annotation { "Feature Type Name" : "Feature", "Feature Type Description" : "" }
export const myFeature = defineFeature(function(context is Context, id is Id, definition is map)
    precondition{}
    {
        {
            var Q0;
            Q0=qCreatedBy(makeId("Front.planeOp"),FACE);
            var sketch = newSketch(context, id + "F0", { "sketchPlane" : qUnion([Q0])});
            skLineSegment(sketch, "E0", {"start": v(-5.6, 6.67) * mm, "end": v(2.01, 6.67) * mm});
            skLineSegment(sketch, "E1", {"start": v(2.01, 6.67) * mm, "end": v(4.63, 8.47) * mm});
            skLineSegment(sketch, "E2", {"start": v(4.63, 8.47) * mm, "end": v(7.83, 9.13) * mm});
            skLineSegment(sketch, "E3", {"start": v(7.83, 9.13) * mm, "end": v(10.2, 8.47) * mm});
            skLineSegment(sketch, "E4", {"start": v(10.2, 8.47) * mm, "end": v(11.6, 6.67) * mm});
            skLineSegment(sketch, "E5", {"start": v(11.6, 6.67) * mm, "end": v(11.6, 3.72) * mm});
            skLineSegment(sketch, "E6", {"start": v(11.6, 3.72) * mm, "end": v(10.2, 1.59) * mm});
            skLineSegment(sketch, "E7.MirrorCS", {"start": v(-5.6, 6.67) * mm, "end": v(-13.23, 6.67) * mm});
            skLineSegment(sketch, "E8.MirrorCS", {"start": v(-13.23, 6.67) * mm, "end": v(-15.85, 8.47) * mm});
            skLineSegment(sketch, "E9.MirrorCS", {"start": v(-15.85, 8.47) * mm, "end": v(-19.05, 9.13) * mm});
            skLineSegment(sketch, "E10.MirrorCS", {"start": v(-19.05, 9.13) * mm, "end": v(-21.42, 8.47) * mm});
            skLineSegment(sketch, "E11.MirrorCS", {"start": v(-21.42, 8.47) * mm, "end": v(-22.82, 6.67) * mm});
            skLineSegment(sketch, "E12.MirrorCS", {"start": v(-22.82, 6.67) * mm, "end": v(-22.82, 3.72) * mm});
            skLineSegment(sketch, "E13.MirrorCS", {"start": v(-22.82, 3.72) * mm, "end": v(-21.42, 1.59) * mm});
            skLineSegment(sketch, "E14.MirrorCS", {"start": v(11.6, -3.72) * mm, "end": v(10.2, -1.59) * mm});
            skLineSegment(sketch, "E15.MirrorCS", {"start": v(11.6, -6.67) * mm, "end": v(11.6, -3.72) * mm});
            skLineSegment(sketch, "E16.MirrorCS", {"start": v(10.2, -8.47) * mm, "end": v(11.6, -6.67) * mm});
            skLineSegment(sketch, "E17.MirrorCS", {"start": v(7.83, -9.13) * mm, "end": v(10.2, -8.47) * mm});
            skLineSegment(sketch, "E18.MirrorCS", {"start": v(4.63, -8.47) * mm, "end": v(7.83, -9.13) * mm});
            skLineSegment(sketch, "E19.MirrorCS", {"start": v(2.01, -6.67) * mm, "end": v(4.63, -8.47) * mm});
            skLineSegment(sketch, "E20.MirrorCS", {"start": v(-5.6, -6.67) * mm, "end": v(2.01, -6.67) * mm});
            skLineSegment(sketch, "E21.MirrorCS", {"start": v(-22.82, -3.72) * mm, "end": v(-21.42, -1.59) * mm});
            skLineSegment(sketch, "E22.MirrorCS", {"start": v(-22.82, -6.67) * mm, "end": v(-22.82, -3.72) * mm});
            skLineSegment(sketch, "E23.MirrorCS", {"start": v(-21.42, -8.47) * mm, "end": v(-22.82, -6.67) * mm});
            skLineSegment(sketch, "E24.MirrorCS", {"start": v(-19.05, -9.13) * mm, "end": v(-21.42, -8.47) * mm});
            skLineSegment(sketch, "E25.MirrorCS", {"start": v(-15.85, -8.47) * mm, "end": v(-19.05, -9.13) * mm});
            skLineSegment(sketch, "E26.MirrorCS", {"start": v(-13.23, -6.67) * mm, "end": v(-15.85, -8.47) * mm});
            skLineSegment(sketch, "E27.MirrorCS", {"start": v(-5.6, -6.67) * mm, "end": v(-13.23, -6.67) * mm});
            skLineSegment(sketch, "E28", {"start": v(10.2, 1.59) * mm, "end": v(9.47, 0) * mm});
            skLineSegment(sketch, "E29", {"start": v(9.47, 0) * mm, "end": v(10.2, -1.59) * mm});
            skLineSegment(sketch, "E30.MirrorCS", {"start": v(-21.42, 1.59) * mm, "end": v(-20.69, 0) * mm});
            skLineSegment(sketch, "E31.MirrorCS", {"start": v(-20.69, 0) * mm, "end": v(-21.42, -1.59) * mm});
            skSolve(sketch);
        }
        {
            var Q0;
            Q0=qSketchRegion(id+"F0",true);
            extrude(context, id + "F1", {"entities" : qUnion([Q0]), "depth" : 2.54 * mm});
        }
        {
            var Q0;
            Q0=makeQuery(id+"F1.opExtrude","CAP_FACE",FACE,{"disambiguationData":[OSD([sQuery(id+"F0.wireOp",EDGE,"E0"),sQuery(id+"F0.wireOp",EDGE,"E1"),sQuery(id+"F0.wireOp",EDGE,"E2"),sQuery(id+"F0.wireOp",EDGE,"E3"),sQuery(id+"F0.wireOp",EDGE,"E4"),sQuery(id+"F0.wireOp",EDGE,"E5"),sQuery(id+"F0.wireOp",EDGE,"E6"),sQuery(id+"F0.wireOp",EDGE,"E7.MirrorCS"),sQuery(id+"F0.wireOp",EDGE,"E8.MirrorCS"),sQuery(id+"F0.wireOp",EDGE,"E9.MirrorCS"),sQuery(id+"F0.wireOp",EDGE,"E10.MirrorCS"),sQuery(id+"F0.wireOp",EDGE,"E11.MirrorCS"),sQuery(id+"F0.wireOp",EDGE,"E12.MirrorCS"),sQuery(id+"F0.wireOp",EDGE,"E13.MirrorCS"),sQuery(id+"F0.wireOp",EDGE,"E14.MirrorCS"),sQuery(id+"F0.wireOp",EDGE,"E15.MirrorCS"),sQuery(id+"F0.wireOp",EDGE,"E16.MirrorCS"),sQuery(id+"F0.wireOp",EDGE,"E17.MirrorCS"),sQuery(id+"F0.wireOp",EDGE,"E18.MirrorCS"),sQuery(id+"F0.wireOp",EDGE,"E19.MirrorCS"),sQuery(id+"F0.wireOp",EDGE,"E20.MirrorCS"),sQuery(id+"F0.wireOp",EDGE,"E21.MirrorCS"),sQuery(id+"F0.wireOp",EDGE,"E22.MirrorCS"),sQuery(id+"F0.wireOp",EDGE,"E23.MirrorCS"),sQuery(id+"F0.wireOp",EDGE,"E24.MirrorCS"),sQuery(id+"F0.wireOp",EDGE,"E25.MirrorCS"),sQuery(id+"F0.wireOp",EDGE,"E26.MirrorCS"),sQuery(id+"F0.wireOp",EDGE,"E27.MirrorCS"),sQuery(id+"F0.wireOp",EDGE,"E28"),sQuery(id+"F0.wireOp",EDGE,"E29"),sQuery(id+"F0.wireOp",EDGE,"E30.MirrorCS"),sQuery(id+"F0.wireOp",EDGE,"E31.MirrorCS")])],"isStart":false});
            var Q1;
            Q1=makeQuery(id+"F1.opExtrude","CAP_EDGE",EDGE,{"disambiguationData":[OSD([sQuery(id+"F0.wireOp",EDGE,"E0"),sQuery(id+"F0.wireOp",EDGE,"E7.MirrorCS")])],"isStart":false});
            var Q2;
            Q2=makeQuery(id+"F1.opExtrude","CAP_EDGE",EDGE,{"disambiguationData":[OSD([sQuery(id+"F0.wireOp",EDGE,"E31.MirrorCS")])],"isStart":false});
            var Q3;
            Q3=makeQuery(id+"F1.opExtrude","CAP_FACE",FACE,{"disambiguationData":[OSD([sQuery(id+"F0.wireOp",EDGE,"E0"),sQuery(id+"F0.wireOp",EDGE,"E1"),sQuery(id+"F0.wireOp",EDGE,"E2"),sQuery(id+"F0.wireOp",EDGE,"E3"),sQuery(id+"F0.wireOp",EDGE,"E4"),sQuery(id+"F0.wireOp",EDGE,"E5"),sQuery(id+"F0.wireOp",EDGE,"E6"),sQuery(id+"F0.wireOp",EDGE,"E7.MirrorCS"),sQuery(id+"F0.wireOp",EDGE,"E8.MirrorCS"),sQuery(id+"F0.wireOp",EDGE,"E9.MirrorCS"),sQuery(id+"F0.wireOp",EDGE,"E10.MirrorCS"),sQuery(id+"F0.wireOp",EDGE,"E11.MirrorCS"),sQuery(id+"F0.wireOp",EDGE,"E12.MirrorCS"),sQuery(id+"F0.wireOp",EDGE,"E13.MirrorCS"),sQuery(id+"F0.wireOp",EDGE,"E14.MirrorCS"),sQuery(id+"F0.wireOp",EDGE,"E15.MirrorCS"),sQuery(id+"F0.wireOp",EDGE,"E16.MirrorCS"),sQuery(id+"F0.wireOp",EDGE,"E17.MirrorCS"),sQuery(id+"F0.wireOp",EDGE,"E18.MirrorCS"),sQuery(id+"F0.wireOp",EDGE,"E19.MirrorCS"),sQuery(id+"F0.wireOp",EDGE,"E20.MirrorCS"),sQuery(id+"F0.wireOp",EDGE,"E21.MirrorCS"),sQuery(id+"F0.wireOp",EDGE,"E22.MirrorCS"),sQuery(id+"F0.wireOp",EDGE,"E23.MirrorCS"),sQuery(id+"F0.wireOp",EDGE,"E24.MirrorCS"),sQuery(id+"F0.wireOp",EDGE,"E25.MirrorCS"),sQuery(id+"F0.wireOp",EDGE,"E26.MirrorCS"),sQuery(id+"F0.wireOp",EDGE,"E27.MirrorCS"),sQuery(id+"F0.wireOp",EDGE,"E28"),sQuery(id+"F0.wireOp",EDGE,"E29"),sQuery(id+"F0.wireOp",EDGE,"E30.MirrorCS"),sQuery(id+"F0.wireOp",EDGE,"E31.MirrorCS")])],"isStart":true});
            fillet(context, id + "F2", {"entities" : qUnion([Q0, Q1, Q2, Q3]), "radius" : 0.5 * mm, "tangentPropagation" : true, "allowEdgeOverflow" : false});
        }
        {
            var Q0;
            Q0=qCreatedBy(makeId("Front.planeOp"),FACE);
            cPlane(context, id + "F3", {"entities" : qUnion([Q0]), "cplaneType" : CPlaneType.OFFSET, "offset" : 1.27 * mm, "width" : 152.4 * mm, "height" : 152.4 * mm});
        }
        {
            var Q0;
            Q0=qCreatedBy(id+"F3.planeOp",FACE);
            var sketch = newSketch(context, id + "F4", { "sketchPlane" : qUnion([Q0])});
            skCircle(sketch, "E32", {"center": v(-5.74, 5.5) * mm, "radius": 1.27 * mm});
            skLineSegment(sketch, "E33", {"start": v(-5.74, 5.5) * mm, "end": v(-5.74, 8.03) * mm});
            skLineSegment(sketch, "E34", {"start": v(-5.74, 8.03) * mm, "end": v(0.39, 8.03) * mm});
            skSolve(sketch);
        }
        {
            var Q0;
            Q0=qSketchRegion(id+"F4",true);
            var Q1;
            Q1=sQuery(id+"F4.wireOp",EDGE,"E34");
            revolve(context, id + "F5", {"operationType" : NewBodyOperationType.ADD, "entities" : qUnion([Q0]), "axis" : qUnion([Q1]), "revolveType" : RevolveType.FULL});
        }
        {
            var Q0;
            Q0=makeQuery(id+"F1.opExtrude","CAP_FACE",FACE,{"disambiguationData":[OSD([sQuery(id+"F0.wireOp",EDGE,"E0"),sQuery(id+"F0.wireOp",EDGE,"E1"),sQuery(id+"F0.wireOp",EDGE,"E2"),sQuery(id+"F0.wireOp",EDGE,"E3"),sQuery(id+"F0.wireOp",EDGE,"E4"),sQuery(id+"F0.wireOp",EDGE,"E5"),sQuery(id+"F0.wireOp",EDGE,"E6"),sQuery(id+"F0.wireOp",EDGE,"E7.MirrorCS"),sQuery(id+"F0.wireOp",EDGE,"E8.MirrorCS"),sQuery(id+"F0.wireOp",EDGE,"E9.MirrorCS"),sQuery(id+"F0.wireOp",EDGE,"E10.MirrorCS"),sQuery(id+"F0.wireOp",EDGE,"E11.MirrorCS"),sQuery(id+"F0.wireOp",EDGE,"E12.MirrorCS"),sQuery(id+"F0.wireOp",EDGE,"E13.MirrorCS"),sQuery(id+"F0.wireOp",EDGE,"E14.MirrorCS"),sQuery(id+"F0.wireOp",EDGE,"E15.MirrorCS"),sQuery(id+"F0.wireOp",EDGE,"E16.MirrorCS"),sQuery(id+"F0.wireOp",EDGE,"E17.MirrorCS"),sQuery(id+"F0.wireOp",EDGE,"E18.MirrorCS"),sQuery(id+"F0.wireOp",EDGE,"E19.MirrorCS"),sQuery(id+"F0.wireOp",EDGE,"E20.MirrorCS"),sQuery(id+"F0.wireOp",EDGE,"E21.MirrorCS"),sQuery(id+"F0.wireOp",EDGE,"E22.MirrorCS"),sQuery(id+"F0.wireOp",EDGE,"E23.MirrorCS"),sQuery(id+"F0.wireOp",EDGE,"E24.MirrorCS"),sQuery(id+"F0.wireOp",EDGE,"E25.MirrorCS"),sQuery(id+"F0.wireOp",EDGE,"E26.MirrorCS"),sQuery(id+"F0.wireOp",EDGE,"E27.MirrorCS"),sQuery(id+"F0.wireOp",EDGE,"E28"),sQuery(id+"F0.wireOp",EDGE,"E29"),sQuery(id+"F0.wireOp",EDGE,"E30.MirrorCS"),sQuery(id+"F0.wireOp",EDGE,"E31.MirrorCS")])],"isStart":false});
            var sketch = newSketch(context, id + "F6", { "sketchPlane" : qUnion([Q0])});
            skText(sketch, "E35", { "text": "Lucy Lou", "fontName": "OpenSans-Regular.ttf"});
            const initialGuessF6  = {"E35": [-0.01677, -0.00217, 1, 0, 0.00392]};
            skSetInitialGuess(sketch, initialGuessF6);
            skSolve(sketch);
        }
        {
            var Q0;
            Q0 = qSketchRegion(id + "F6", true);
            extrude(context, id + "F7", {"entities" : qUnion([Q0]), "operationType" : NewBodyOperationType.REMOVE, "oppositeDirection" : true, "depth" : 1.27 * mm});
        }
    });